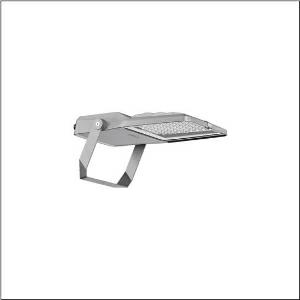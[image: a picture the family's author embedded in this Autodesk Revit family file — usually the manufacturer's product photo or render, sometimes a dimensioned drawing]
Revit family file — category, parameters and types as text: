
# Revit family: floodlight_fl_21_mini___pl43_5xa7772c3a1a_c6a2
name_source: partatom
category: Lighting Fixtures
units: mm (PartAtom-declared; Revit-internal decimal feet)

## family parameters
Cut with Voids When Loaded = No
Host = Face
Light Source = No
Part Type = Normal
Room Calculation Point = No
Round Connector Dimension = Use Diameter
Shared = No

## types (1)
- --- (1 x LED, 10780 lm, 87.2 W, 3000K)
    Apparent Load = 87 VA
    CIE Flux Codes = 27 78 99 100 100
    Color Rendering = 80
    Color Temperature = 3000K
    Default Elevation = 1800 mm
    Description = Floodlight FL 21 mini, floodlight, primary light control with lens, of PMMA, primary optical cover: protective disc, of toughened safety glass, transparent, light distribution: PL43, light emission: direct distribution, installation type: surface-mounted, LED, High Power LED, rated luminous flux: 10.780lm, luminous efficacy: 124lm/W, light colour: 830, colour temperature: 3000K, control gear: ECG iQ, control: Street-Remote, Auto-Match, Temp-Guard, Night-Set, Smart-Wire, Desk-Remote (wireless, voltage-free reading and setting of iQ features in the workshop via application-optimized NFC function/RFID function), optimised constant luminous flux control (CLO 2.0), with terminal, 6-pole, mains connection: 220..240V, AC, 50/60Hz, start of lifetime: 87W, end of lifetime: 92W, reduction: 40W, luminaire housing, of diecast aluminium, powder-coated, Siteco® metallic grey (DB 702S), corrosivity category C5 according to DIN EN ISO 12944, mounting bracket, of steel, galvanised, powder-coated, Siteco® metallic grey (DB 702S), protection rating (complete): IP66, insulation class (complete): insulation class II (safety insulation), certification: CE, ENEC, VDE, protection symbol: D, impact resistance: IK08, permissible operating ambient temperature: -40..+40°C, permissible operating ambient temperature for outdoor applications: -40..+50°C, standard: DIN EN 12944, packaging unit: 1 piece

Light Distribution: PL43
    Height = 70 mm
    Lamp = 1 x LED
    Lamp Light Flux = 10780 lm
    Lamp Power = 87.2 W
    Lamp count = 1
    Length = 485 mm
    Luminous efficacy = 124 lm/W
    Manufacturer = Siteco
    ModVariant = No
    Model = 5XA7772C3A1A
    Number of Poles = 1
    OnlyDefault = Yes
    Power Factor = 1
    Product Name = Floodlight FL 21 mini | PL43
    Product group = floodlight | pylon top
    ProductGroupID = 6101
    Protection Class = Protection class II
    Protection Degree = IP 66
    RLX_Detail_Level = 1
    RlxData = <blob elided: 96029 chars, md5=92341c04>
    Socket = socket
    Standby Power = 0 W
    System Light Flux = 10780 lm
    System Power = 87 W
    Type Comments = factory setting: luminous flux: 100 % | dim-lin: 254 | 456 mA
    Type Image = l_1006845.jpg
    URL = http://relux.com
    VarID = @adj_073457
    Voltage = 0 V
    Weight = 0.00 kg
    Width = 337 mm

## geometry (parser evidence)
native form markers: Blend x4, Sweep x12
no freeform markers — native parametric forms only
